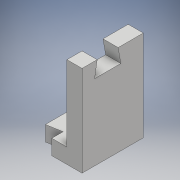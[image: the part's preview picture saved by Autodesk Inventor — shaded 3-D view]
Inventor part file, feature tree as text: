
AUTODESK INVENTOR PART (.ipt)
format: ipt  version: 2017 (Build 210142000, 142)  size: 347,648 bytes
history: native  units: mm
features: extrude x28, sketch x28, shell x1
ambient origin geometry x8: Origin, YZ Plane, XZ Plane, XY Plane, X Axis, Y Axis, Z Axis, Center Point
bodies: Solid1 (feature_tree)
feature tree (57):
  extrude  "Extrusion1"  Depth=20.0mm
  shell  "Shell1"  Thickness=20.0mm
  extrude  "Extrusion2"  Depth=55.0mm
  extrude  "Extrusion3"  TaperAngle=0.0deg  [1 undecoded]
  extrude  "Extrusion4"  Depth=5.0mm
  extrude  "Extrusion5"  TaperAngle=0.0deg  [1 undecoded]
  extrude  "Extrusion6"  Depth=10.0mm TaperAngle=0.0deg
  extrude  "Extrusion7"  Depth=15.0mm TaperAngle=0.0deg
  extrude  "Extrusion9"  Depth=8.5mm
  extrude  "Extrusion10"  Depth=15.0mm TaperAngle=0.0deg
  extrude  "Extrusion11"  Depth=35.46mm
  extrude  "Extrusion12"  Depth=15.0mm TaperAngle=0.0deg
  extrude  "Extrusion13"  Depth=4.5mm
  extrude  "Extrusion14"  Depth=15.0mm TaperAngle=0.0deg
  extrude  "Extrusion15"  Depth=8.5mm
  extrude  "Extrusion16"  Depth=15.0mm TaperAngle=0.0deg
  extrude  "Extrusion17"  Depth=28.505mm
  extrude  "Extrusion18"  Depth=15.0mm TaperAngle=0.0deg
  extrude  "Extrusion19"  Depth=36.0mm
  extrude  "Extrusion20"  Depth=15.0mm TaperAngle=0.0deg
  extrude  "Extrusion21"  Depth=5.0mm
  extrude  "Extrusion22"  Depth=4.1656mm
  extrude  "Extrusion23"  Depth=35.46mm
  extrude  "Extrusion24"  Depth=10.0mm
  extrude  "Extrusion25"  Depth=10.0mm TaperAngle=0.0deg
  extrude  "Extrusion26"  Depth=2.583mm TaperAngle=0.0deg
  extrude  "Extrusion27"  Depth=2.583mm TaperAngle=0.0deg
  extrude  "Extrusion28"  Depth=100.0mm TaperAngle=0.0deg
  extrude  "Extrusion29"  Depth=5.0mm
  sketch  "Sketch1"  dims[d0=35.0mm d1=37.0mm d2=20.0mm]
  sketch  "Sketch2"  dims[d3=11.0mm d4=55.0mm]
  sketch  "Sketch3"  dims[d5=26.0mm d6=0.0mm]
  sketch  "Sketch4"  dims[d7=50.0mm d8=0.0mm d9=5.0mm]
  sketch  "Sketch5"  dims[d10=17.0mm d11=0.0mm]
  sketch  "Sketch6"  dims[d12=11.0mm d13=10.0mm d14=0.0mm]
  sketch  "Sketch7"  dims[d15=15.0mm d16=0.0mm d17=15.0mm d18=0.0mm]
  sketch  "Sketch13"  dims[d19=4.1656mm d20=8.5mm]
  sketch  "Sketch14"  dims[d21=11.5mm d22=15.0mm d23=0.0mm]
  sketch  "Sketch15"  dims[d24=4.1656mm d25=35.46mm]
  sketch  "Sketch16"  dims[d26=23.505mm d27=15.0mm d28=0.0mm]
  sketch  "Sketch17"  dims[d29=4.1656mm d30=4.5mm]
  sketch  "Sketch18"  dims[d31=14.0mm d32=15.0mm d33=0.0mm]
  sketch  "Sketch20"  dims[d41=4.1656mm d42=8.5mm]
  sketch  "Sketch21"  dims[d43=11.5mm d44=15.0mm d45=0.0mm]
  sketch  "Sketch22"  dims[d46=4.1656mm d47=28.505mm]
  sketch  "Sketch23"  dims[d48=35.46mm d49=15.0mm d50=0.0mm]
  sketch  "Sketch24"  dims[d51=4.1656mm d52=36.0mm]
  sketch  "Sketch25"  dims[d53=4.5mm d54=15.0mm d55=0.0mm]
  sketch  "Sketch29"  dims[d63=10.0mm d64=0.0mm d65=4.1656mm]
  sketch  "Sketch31"  dims[d67=36.0mm d68=10.0mm d69=0.0mm]
  sketch  "Sketch33"  dims[d73=2.583mm d74=0.0mm d75=2.583mm d76=0.0mm]
  sketch  "Sketch34"  dims[d77=6.917mm d78=100.0mm d79=0.0mm]
  sketch  "Sketch35"  dims[d80=5.0mm d81=5.0mm d83=1.0mm d84=1.0mm d85=100.0mm d86=0.0mm d87=5.0mm d88=100.0mm d89=0.0mm d90=8.6943mm d91=13.962634mm d92=29.670597mm d93=0.0mm d94=5.0mm d96=100.0mm d97=0.0mm d98=8.6943mm d99=13.962634mm d100=29.670597mm d102=5.0mm d104=0.0mm d105=26.08299mm d106=8.6943mm d107=13.962634mm d108=29.670597mm d109=5.0mm d112=5.0mm d113=0.0mm d114=5.0mm d115=0.0mm d116=100.0mm d117=0.0mm d118=100.0mm d119=0.0mm d120=8.6943mm d121=13.962634mm d122=29.670597mm d123=5.0mm d124=0.0mm d125=8.69433mm d126=5.0mm d127=0.0mm d128=7.437911mm d130=22.832mm d131=10.0mm d132=0.0mm d133=5.0mm d134=5.0mm d135=0.0mm d136=5.077mm d137=1.745329mm d138=5.077mm d139=3.744mm d140=6.931mm d141=5.0mm d142=0.0mm]
  sketch  "Sketch27"  dims[d58=21.0mm d59=0.0mm d60=4.1656mm]
  sketch  "Sketch28"  dims[d61=23.505mm d62=35.46mm]
  sketch  "Sketch26"  dims[d56=5.0mm d57=50.0mm]
  sketch  "Sketch32"  dims[d70=4.5mm d71=2.583mm d72=0.0mm]
note: 2 required parameter values undecoded (feature->parameter linkage not recoverable at this tier; creation-order binding heuristic only, values carry confidence <= 0.55)
